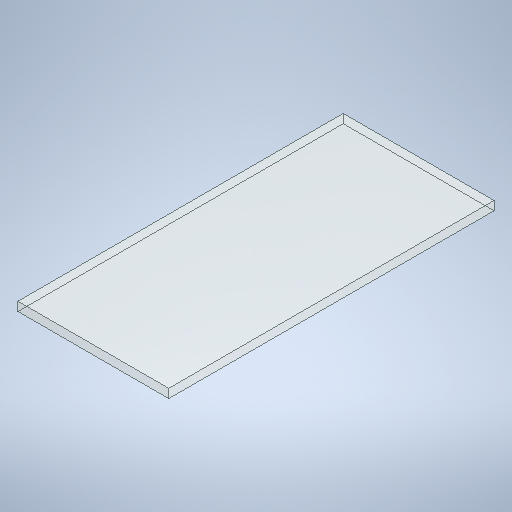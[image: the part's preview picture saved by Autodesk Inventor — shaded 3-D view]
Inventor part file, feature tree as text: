
AUTODESK INVENTOR PART (.ipt)
format: ipt  version: 2025.2 (Build 292293000, 293)  size: 236,544 bytes
history: native  units: in
note: dims shown in document units (in); Inventor stores cm internally (conversion verified against a paired STEP export)
features: extrude x1, sketch x1
ambient origin geometry x8: Origin, YZ Plane, XZ Plane, XY Plane, X Axis, Y Axis, Z Axis, Center Point
bodies: Solid1 (feature_tree)
feature tree (2):
  extrude  "Extrusion1"  Depth=4.3307in
  sketch  "Sketch1"  dims[d0=2.0079in d1=4.3307in d2=0.1181in d3=0.0in]
